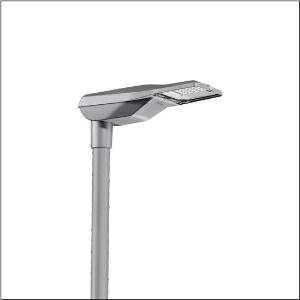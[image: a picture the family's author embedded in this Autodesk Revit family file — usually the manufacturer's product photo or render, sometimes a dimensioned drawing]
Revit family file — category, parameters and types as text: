
# Revit family: streetlight_sl_21_iq_micro___st1_5a_5xe1p31g08cb_4914
name_source: partatom
category: Lighting Fixtures
units: mm (PartAtom-declared; Revit-internal decimal feet)

## family parameters
Cut with Voids When Loaded = No
Host = Face
Light Source = No
Part Type = Normal
Room Calculation Point = No
Round Connector Dimension = Use Diameter
Shared = No

## types (1)
- --- (1 x LED, 2820 lm, 19.4 W, 3000K)
    Apparent Load = 19 VA
    CIE Flux Codes = 22 53 95 100 100
    Color Rendering = 70
    Color Temperature = 3000K
    Default Elevation = 1800 mm
    Description = Streetlight SL 21 iQ micro, mast luminaire, primary light control with lens, of PMMA, primary optical cover: cover, of toughened safety glass, transparent, light distribution: ST1.5a, light emission: direct distribution, primary light characteristic: asymmetric, installation type: post-top, side-entry, LED, High Power LED, rated luminous flux: 2.820lm, luminous efficacy: 145lm/W, light colour: 730, colour temperature: 3000K, control: Street-Remote, Auto-Match, Temp-Guard, Lumen-Switch, Night-Set, Smart-Wire, Light-Fading, Desk-Remote (wireless, voltage-free reading and setting of iQ features in the workshop via application-optimized NFC function/RFID function), optimised constant luminous flux control (CLO 2.0), presetting dimming linear, mains connection: 220..240V, AC, 50/60Hz, start of lifetime: 19W, end of service life: 20W, reduction: 10W, luminaire housing, of diecast aluminium, powder-coated, Siteco® metallic grey (DB 702S), corrosivity category C5 mid according to DIN EN ISO 12944, please order mast flange separately, inclination adjustable: 0°, 5°, 10°, 15°, sealing non-destructively replaceable, multi-level sealing system, length: 528mm, width: 235mm, height: 110mm, mast flange for spigot size: 42mm (side-entry): 5XC10008XM4, 60/48mm (side-entry/post-top): 5XC10108XM2, 76/60mm (side-entry/post-top): 5XC10108XM1, protection rating (complete): IP66, insulation class (complete): insulation class II (safety insulation), certification: CE, ENEC, ENEC+, VDE, impact resistance: IK09, permissible operating ambient temperature for outdoor applications: -40..+50°C, standard-compliant lighting for roads and squares, packaging unit: 1 piece

Light Distribution: ST1.5a
    Height = 110 mm
    Lamp = 1 x LED
    Lamp Light Flux = 2820 lm
    Lamp Power = 19.4 W
    Lamp count = 1
    Length = 528 mm
    Luminous efficacy = 145 lm/W
    Manufacturer = Siteco
    ModVariant = No
    Model = 5XE1P31G08CB
    Number of Poles = 1
    OnlyDefault = Yes
    Power Factor = 1
    Product Name = Streetlight SL 21 iQ micro | ST1.5a
    Product group = mast luminaire | pylon top
    ProductGroupID = 6100
    Protection Class = Protection class II
    Protection Degree = IP 66
    RLX_Detail_Level = 1
    RLX_Emergency_Light_Flux = 0 lm
    RLX_Emergency_Type = 0
    RLX_Emergency_Type_DB = No
    RlxData = <blob elided: 103601 chars, md5=f3793e9b>
    Socket = socket
    Standby Power = 0 W
    System Light Flux = 2820 lm
    System Power = 19 W
    Type Comments = factory setting: luminous flux: 100 % | dim-lin: 254 | 387 mA
    Type Image = l_1006881.jpg
    URL = http://relux.com
    VarID = @adj_087441
    Voltage = 0 V
    Weight = 0.00 kg
    Width = 235 mm

## geometry (parser evidence)
native form markers: Blend x4, Sweep x12
no freeform markers — native parametric forms only
